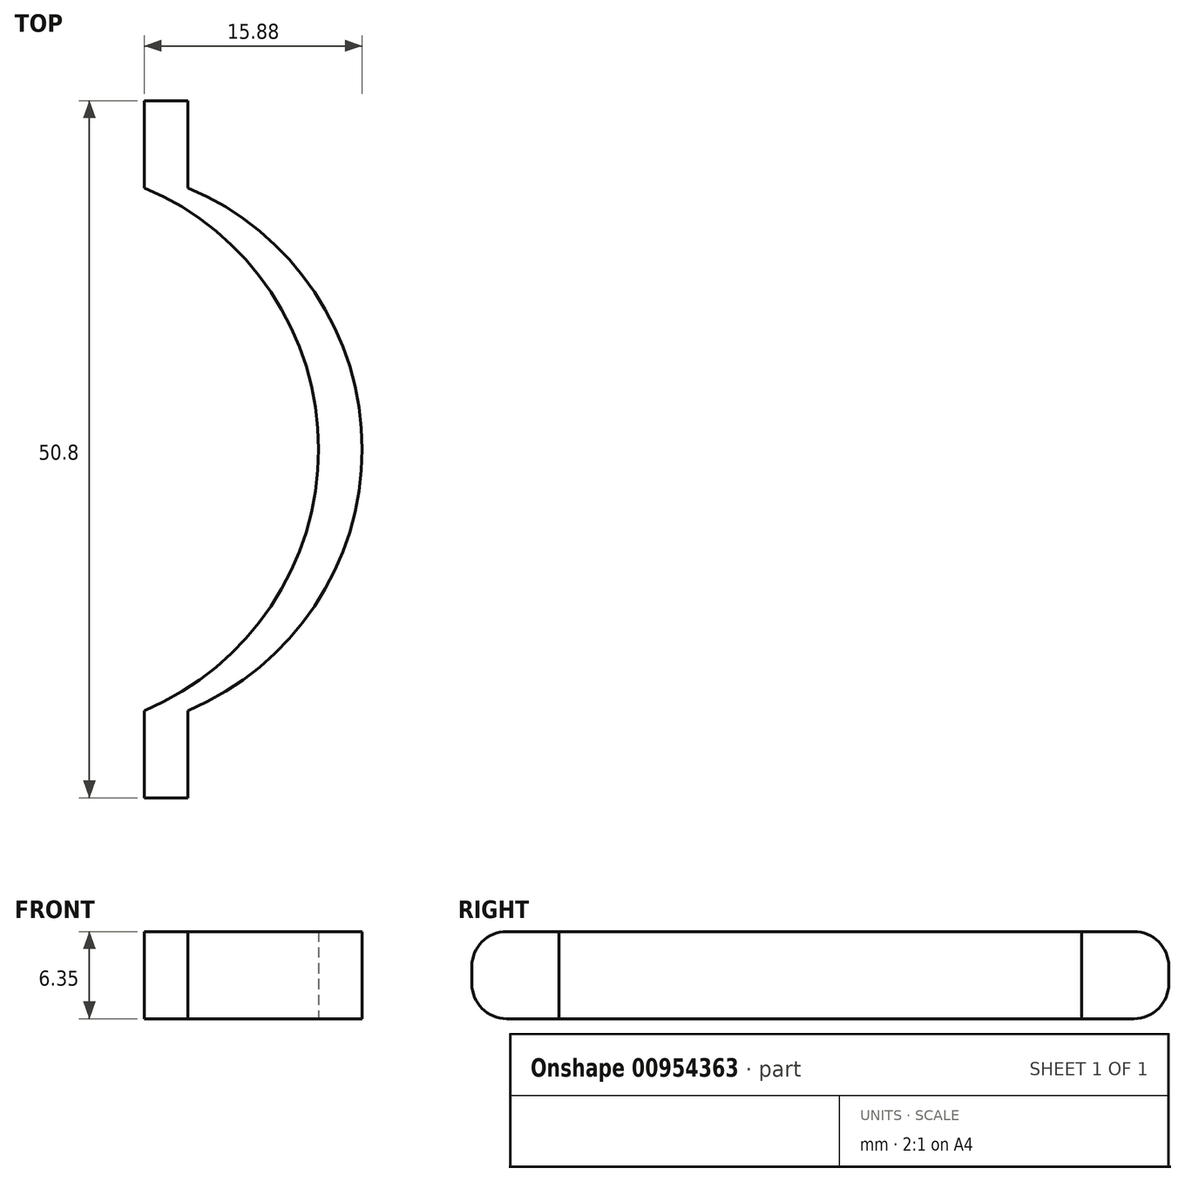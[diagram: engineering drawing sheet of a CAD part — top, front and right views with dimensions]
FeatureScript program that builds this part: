
annotation { "Feature Type Name" : "Feature", "Feature Type Description" : "" }
export const myFeature = defineFeature(function(context is Context, id is Id, definition is map)
    precondition{}
    {
        {
            var Q0;
            Q0=qCreatedBy(makeId("Top.planeOp"),FACE);
            var sketch = newSketch(context, id + "F0", { "sketchPlane" : qUnion([Q0])});
            skArc(sketch, "E0", {"start": v(0, -18.78) * mm, "mid": v(12.7, 0.27) * mm, "end": v(0, 19.32) * mm});
            skLineSegment(sketch, "E1", {"start": v(0, 19.32) * mm, "end": v(0, 25.67) * mm});
            skLineSegment(sketch, "E2", {"start": v(0, 25.67) * mm, "end": v(3.17, 25.67) * mm});
            skLineSegment(sketch, "E3", {"start": v(3.17, 25.67) * mm, "end": v(3.18, 19.32) * mm});
            skLineSegment(sketch, "E4", {"start": v(0, -18.78) * mm, "end": v(0, -25.13) * mm});
            skLineSegment(sketch, "E5", {"start": v(0, -25.13) * mm, "end": v(3.18, -25.13) * mm});
            skLineSegment(sketch, "E6", {"start": v(3.18, -25.13) * mm, "end": v(3.18, -18.78) * mm});
            skArc(sketch, "E7", {"start": v(3.17, -18.78) * mm, "mid": v(15.88, 0.27) * mm, "end": v(3.17, 19.32) * mm});
            skSolve(sketch);
        }
        {
            var Q0;
            Q0=makeQuery(id+"F0.imprint","IMPRINT",FACE,{"disambiguationData":[TD([[makeQuery(id+"F0.imprint","IMPRINT",EDGE,{"derivedFrom":sQuery(id+"F0.wireOp",EDGE,"E0")}),-1.0]])]});
            extrude(context, id + "F1", {"entities" : qUnion([Q0]), "depth" : 6.35 * mm, "offsetDistance" : 25.4 * mm});
        }
        {
            var Q0;
            Q0=makeQuery(id+"F1.opExtrude","CAP_EDGE",EDGE,{"disambiguationData":[OSD([sQuery(id+"F0.wireOp",EDGE,"E5")])],"isStart":false});
            var Q1;
            Q1=makeQuery(id+"F1.opExtrude","CAP_EDGE",EDGE,{"disambiguationData":[OSD([sQuery(id+"F0.wireOp",EDGE,"E5")])],"isStart":true});
            var Q2;
            Q2=makeQuery(id+"F1.opExtrude","CAP_EDGE",EDGE,{"disambiguationData":[OSD([sQuery(id+"F0.wireOp",EDGE,"E2")])],"isStart":true});
            var Q3;
            Q3=makeQuery(id+"F1.opExtrude","CAP_EDGE",EDGE,{"disambiguationData":[OSD([sQuery(id+"F0.wireOp",EDGE,"E2")])],"isStart":false});
            fillet(context, id + "F2", {"entities" : qUnion([Q0, Q1, Q2, Q3]), "radius" : 2.54 * mm, "tangentPropagation" : true, "allowEdgeOverflow" : false});
        }
    });
